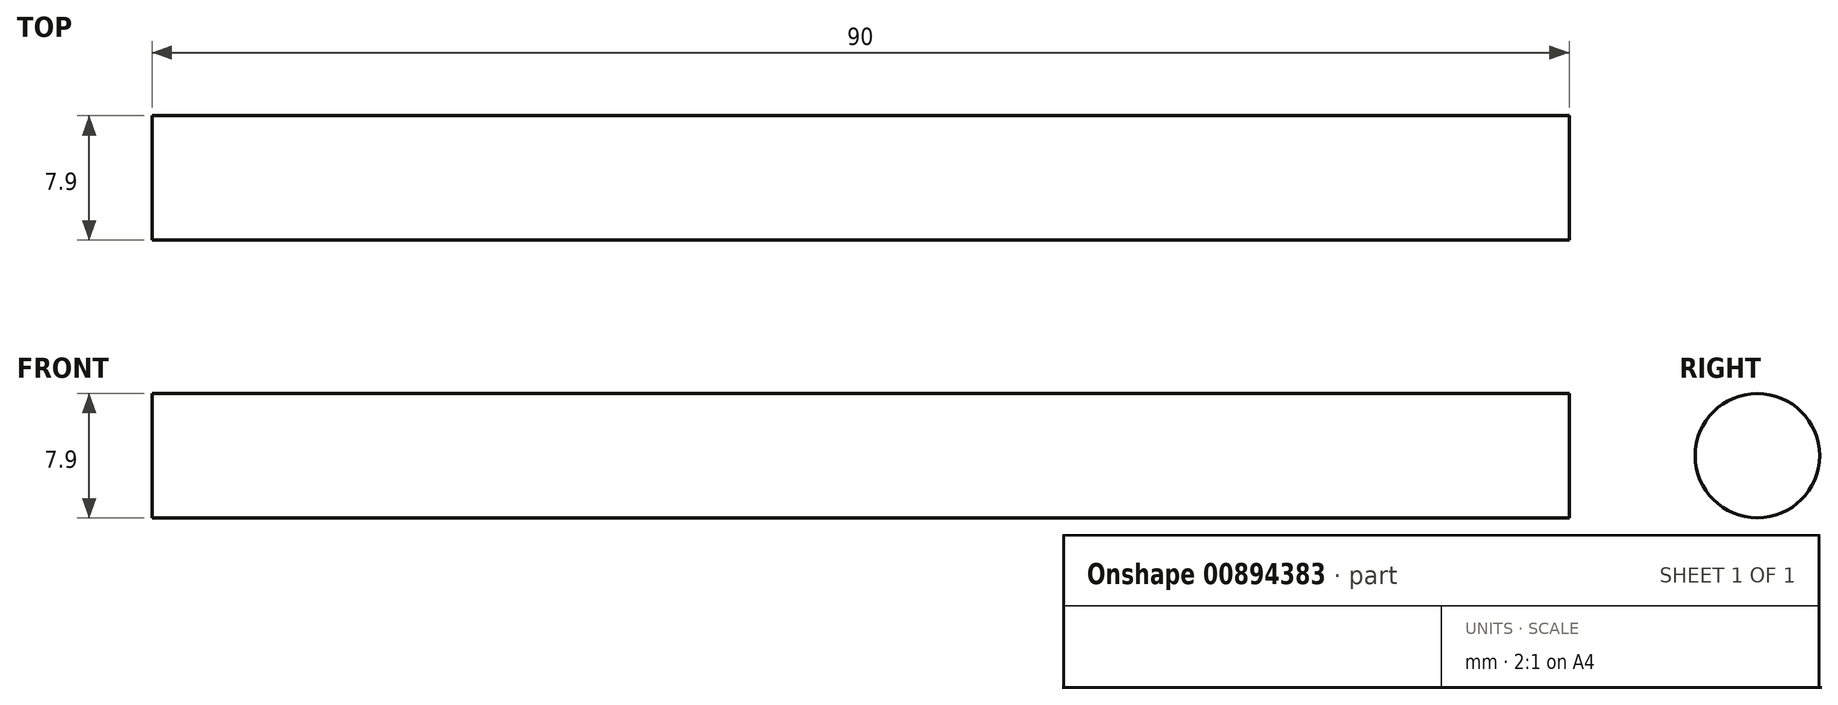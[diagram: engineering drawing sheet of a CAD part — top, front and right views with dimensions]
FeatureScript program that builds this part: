
annotation { "Feature Type Name" : "Feature", "Feature Type Description" : "" }
export const myFeature = defineFeature(function(context is Context, id is Id, definition is map)
    precondition{}
    {
        {
            var Q0;
            Q0=qCreatedBy(makeId("Right.planeOp"),FACE);
            var sketch = newSketch(context, id + "F0", { "sketchPlane" : qUnion([Q0])});
            skCircle(sketch, "E0", {"center": v(0, 0) * mm, "radius": 3.95 * mm});
            skSolve(sketch);
        }
        {
            var Q0;
            Q0 = qSketchRegion(id + "F0", true);
            extrude(context, id + "F1", {"entities" : qUnion([Q0]), "endBound" : BoundingType.SYMMETRIC, "depth" : 90 * mm, "offsetDistance" : 25 * mm});
        }
    });
